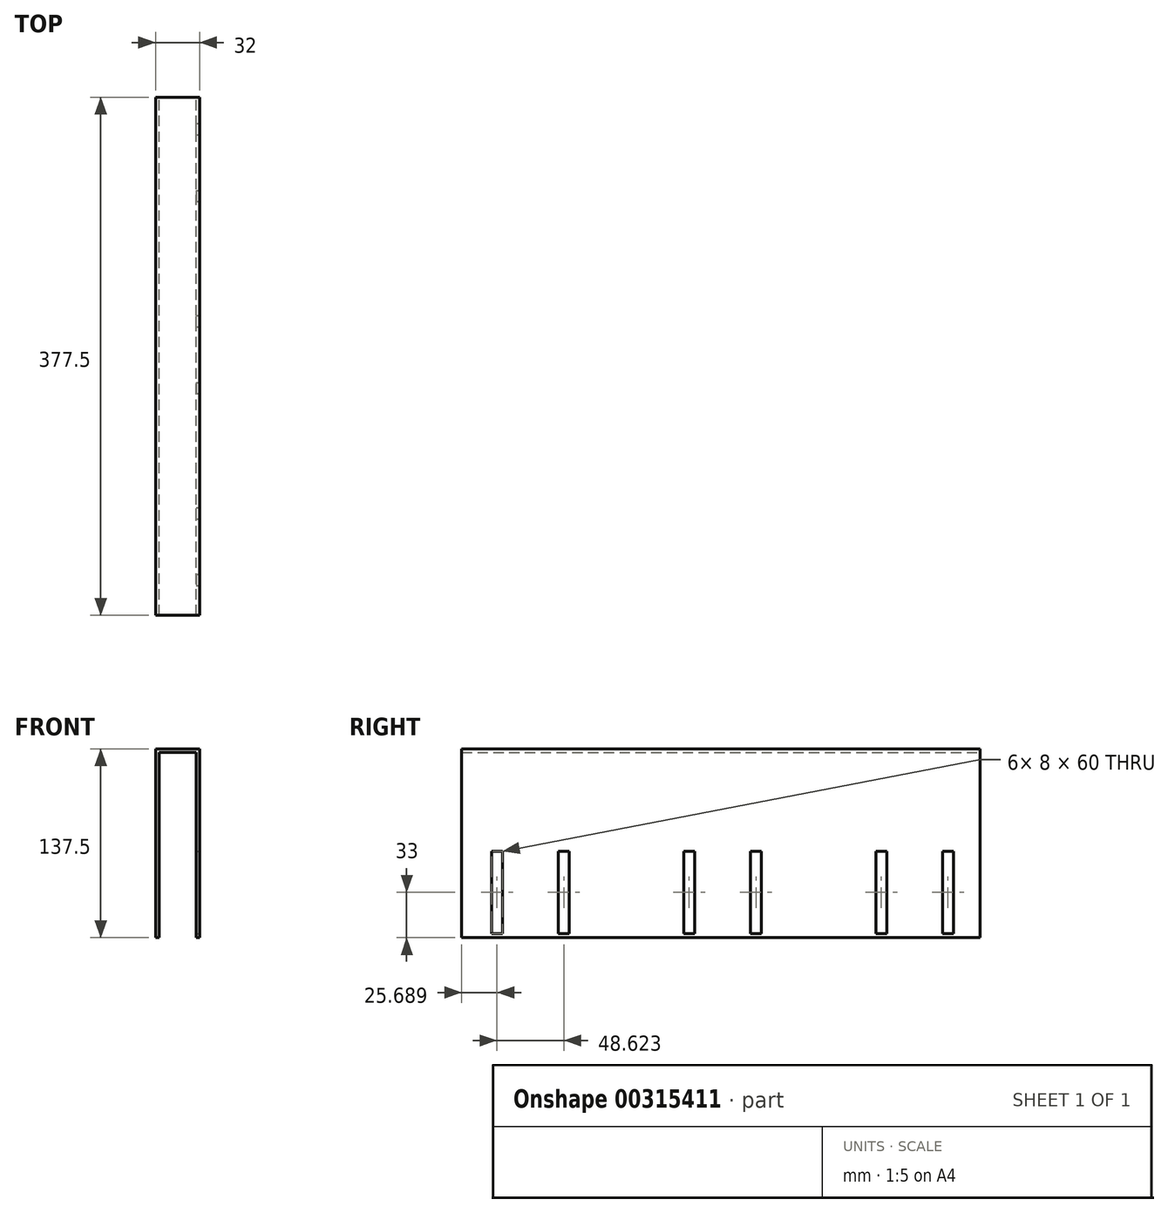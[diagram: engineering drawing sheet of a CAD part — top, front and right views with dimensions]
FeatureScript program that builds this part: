
annotation { "Feature Type Name" : "Feature", "Feature Type Description" : "" }
export const myFeature = defineFeature(function(context is Context, id is Id, definition is map)
    precondition{}
    {
        {
            var Q0;
            Q0=qCreatedBy(makeId("Right.planeOp"),FACE);
            var sketch = newSketch(context, id + "F0", { "sketchPlane" : qUnion([Q0])});
            skLineSegment(sketch, "E0.bottom", {"start": v(-190, -70) * mm, "end": v(190, -70) * mm});
            skLineSegment(sketch, "E0.top", {"start": v(-190, 70) * mm, "end": v(190, 70) * mm});
            skLineSegment(sketch, "E0.left", {"start": v(-190, -70) * mm, "end": v(-190, 70) * mm});
            skLineSegment(sketch, "E0.right", {"start": v(190, -70) * mm, "end": v(190, 70) * mm});
            skPoint(sketch, "E0.middle", {"position": v(0, 0) * mm});
            skSolve(sketch);
        }
        {
            var Q0;
            Q0=makeQuery(id+"F0.imprint","IMPRINT",FACE,{"disambiguationData":[TD([[makeQuery(id+"F0.imprint","IMPRINT",EDGE,{"derivedFrom":sQuery(id+"F0.wireOp",EDGE,"E0.bottom")}),1.0]])]});
            extrude(context, id + "F1", {"entities" : qUnion([Q0]), "depth" : 32 * mm});
        }
        {
            var Q0;
            Q0=makeQuery(id+"F1.opExtrude","SWEPT_FACE",FACE,{"disambiguationData":[OSD([sQuery(id+"F0.wireOp",EDGE,"E0.left")])]});
            shell(context, id + "F2", {"entities" : qUnion([Q0]), "thickness" : 2.5 * mm});
        }
        {
            var Q0;
            Q0=makeQuery(id+"F1.opExtrude","SWEPT_FACE",FACE,{"disambiguationData":[OSD([sQuery(id+"F0.wireOp",EDGE,"E0.bottom")])]});
            extrude(context, id + "F3", {"entities" : qUnion([Q0]), "operationType" : NewBodyOperationType.REMOVE, "oppositeDirection" : true, "depth" : 2.5 * mm});
        }
        {
            var Q0;
            Q0=makeQuery(id+"F1.opExtrude","SWEPT_FACE",FACE,{"disambiguationData":[OSD([sQuery(id+"F0.wireOp",EDGE,"E0.right")])]});
            extrude(context, id + "F4", {"entities" : qUnion([Q0]), "operationType" : NewBodyOperationType.REMOVE, "oppositeDirection" : true, "depth" : 2.5 * mm});
        }
        {
            var Q0;
            Q0=makeQuery(id+"F1.opExtrude","CAP_FACE",FACE,{"disambiguationData":[OSD([sQuery(id+"F0.wireOp",EDGE,"E0.bottom"),sQuery(id+"F0.wireOp",EDGE,"E0.top"),sQuery(id+"F0.wireOp",EDGE,"E0.left"),sQuery(id+"F0.wireOp",EDGE,"E0.right")])],"isStart":false});
            var sketch = newSketch(context, id + "F5", { "sketchPlane" : qUnion([Q0])});
            skLineSegment(sketch, "E1.bottom", {"start": v(-168.31, -64.5) * mm, "end": v(-160.31, -64.5) * mm});
            skLineSegment(sketch, "E1.top", {"start": v(-168.31, -4.5) * mm, "end": v(-160.31, -4.5) * mm});
            skLineSegment(sketch, "E1.left", {"start": v(-168.31, -64.5) * mm, "end": v(-168.31, -4.5) * mm});
            skLineSegment(sketch, "E1.right", {"start": v(-160.31, -64.5) * mm, "end": v(-160.31, -4.5) * mm});
            skLineSegment(sketch, "E2", {"start": v(-140, 70) * mm, "end": v(-140, -67.5) * mm, "construction": true});
            skLineSegment(sketch, "E3", {"start": v(0, 70.14) * mm, "end": v(0, -67.36) * mm, "construction": true});
            skLineSegment(sketch, "E4", {"start": v(-70, 69.87) * mm, "end": v(-70, -67.63) * mm, "construction": true});
            skLineSegment(sketch, "E5.MirrorCS", {"start": v(-111.69, -64.5) * mm, "end": v(-111.69, -4.5) * mm});
            skLineSegment(sketch, "E6.MirrorCS", {"start": v(-119.69, -64.5) * mm, "end": v(-119.69, -4.5) * mm});
            skLineSegment(sketch, "E7.MirrorCS", {"start": v(-111.69, -4.5) * mm, "end": v(-119.69, -4.5) * mm});
            skLineSegment(sketch, "E8.MirrorCS", {"start": v(-111.69, -64.5) * mm, "end": v(-119.69, -64.5) * mm});
            skLineSegment(sketch, "E9.MirrorCS", {"start": v(28.31, -64.5) * mm, "end": v(20.31, -64.5) * mm});
            skLineSegment(sketch, "E10.MirrorCS", {"start": v(-28.31, -64.5) * mm, "end": v(-28.31, -4.5) * mm});
            skLineSegment(sketch, "E11.MirrorCS", {"start": v(28.31, -64.5) * mm, "end": v(28.31, -4.5) * mm});
            skLineSegment(sketch, "E12.MirrorCS", {"start": v(20.31, -64.5) * mm, "end": v(20.31, -4.5) * mm});
            skLineSegment(sketch, "E13.MirrorCS", {"start": v(-20.31, -64.5) * mm, "end": v(-20.31, -4.5) * mm});
            skLineSegment(sketch, "E14.MirrorCS", {"start": v(-28.31, -64.5) * mm, "end": v(-20.31, -64.5) * mm});
            skLineSegment(sketch, "E15.MirrorCS", {"start": v(28.31, -4.5) * mm, "end": v(20.31, -4.5) * mm});
            skLineSegment(sketch, "E16.MirrorCS", {"start": v(-28.31, -4.5) * mm, "end": v(-20.31, -4.5) * mm});
            skLineSegment(sketch, "E17.MirrorCS", {"start": v(168.31, -64.5) * mm, "end": v(160.31, -64.5) * mm});
            skLineSegment(sketch, "E18.MirrorCS", {"start": v(111.69, -64.5) * mm, "end": v(111.69, -4.5) * mm});
            skLineSegment(sketch, "E19.MirrorCS", {"start": v(119.69, -64.5) * mm, "end": v(119.69, -4.5) * mm});
            skLineSegment(sketch, "E20.MirrorCS", {"start": v(168.31, -4.5) * mm, "end": v(160.31, -4.5) * mm});
            skLineSegment(sketch, "E21.MirrorCS", {"start": v(160.31, -64.5) * mm, "end": v(160.31, -4.5) * mm});
            skLineSegment(sketch, "E22.MirrorCS", {"start": v(111.69, -4.5) * mm, "end": v(119.69, -4.5) * mm});
            skLineSegment(sketch, "E23.MirrorCS", {"start": v(111.69, -64.5) * mm, "end": v(119.69, -64.5) * mm});
            skLineSegment(sketch, "E24.MirrorCS", {"start": v(168.31, -64.5) * mm, "end": v(168.31, -4.5) * mm});
            skSolve(sketch);
        }
        {
            var Q0;
            Q0 = qSketchRegion(id + "F5", true);
            var Q1;
            {var subQ0=sQuery(id+"F0.wireOp",EDGE,"E0.right");var subQ1=sQuery(id+"F0.wireOp",EDGE,"E0.left");var subQ2=sQuery(id+"F0.wireOp",EDGE,"E0.top");var subQ3=sQuery(id+"F0.wireOp",EDGE,"E0.bottom");Q1=makeQuery(id+"F2.opShell","OFFSET_FACE",FACE,{"disambiguationData":[OSD([subQ3,subQ2,subQ1,subQ0]),TDD([makeQuery(id+"F1.opExtrude","CAP_FACE",FACE,{"disambiguationData":[OSD([subQ3,subQ2,subQ1,subQ0])],"isStart":false})])]});}
            extrude(context, id + "F6", {"entities" : qUnion([Q0]), "operationType" : NewBodyOperationType.REMOVE, "endBound" : BoundingType.UP_TO_SURFACE, "oppositeDirection" : true, "endBoundEntityFace" : qUnion([Q1]), "depth" : 25 * mm});
        }
    });
